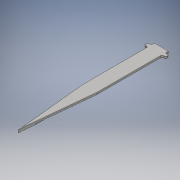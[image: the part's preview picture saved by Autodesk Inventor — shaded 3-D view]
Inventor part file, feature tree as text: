
AUTODESK INVENTOR PART (.ipt)
format: ipt  version: 2016 (Build 200138000, 138)  size: 243,712 bytes
history: native  units: mm
features: fillet x3, extrude x2, sketch x2, other x1
ambient origin geometry x8: Origin, YZ Plane, XZ Plane, XY Plane, X Axis, Y Axis, Z Axis, Center Point
bodies: Solid1 (feature_tree)
feature tree (8):
  other  "<userpath>\Documents\GitHub\3D\Hoja Oculta\Parametros.xlsx"
  extrude  "Cuerpo"  Depth=200.0mm
  extrude  "Rail"  Depth=0.5mm
  fillet  "Biselado tope"  Radius=5.0mm
  fillet  "Biselado cola"  Radius=5.0mm
  fillet  "Biselado filo"  Radius=5.0mm
  sketch  "Sketch2"  dims[d0=20.0mm d1=200.0mm]
  sketch  "Sketch3"  dims[d2=100.0mm d3=5.0mm d4=5.0mm d5=5.0mm d6=5.0mm d7=5.0mm d8=5.0mm d9=3.0mm d10=0.0mm d11=4.4mm d12=1.2mm d13=0.0mm d14=2.0mm d16=1.0mm d17=0.5mm]
